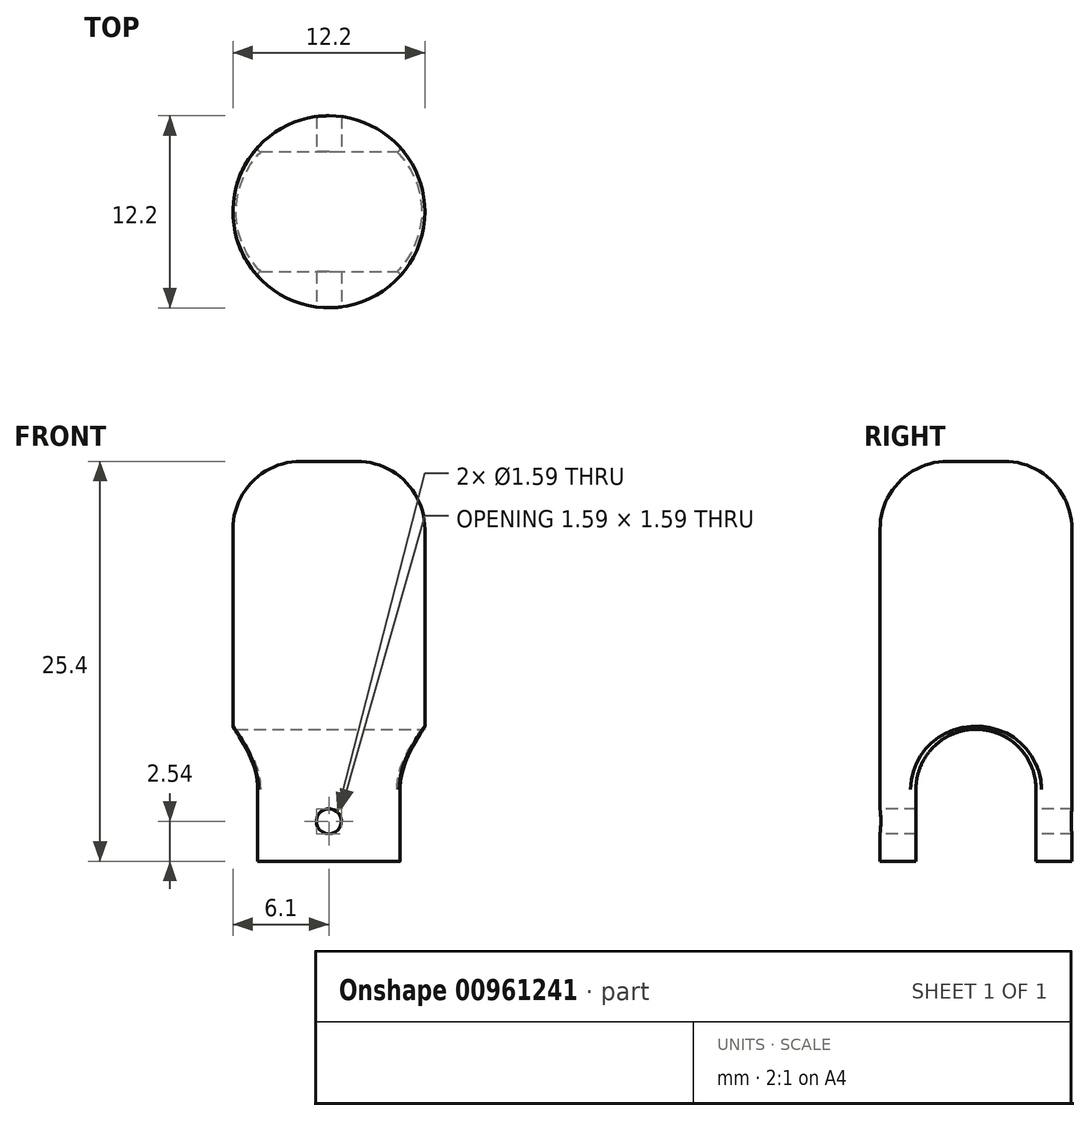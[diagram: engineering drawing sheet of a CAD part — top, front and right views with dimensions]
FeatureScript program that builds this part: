
annotation { "Feature Type Name" : "Feature", "Feature Type Description" : "" }
export const myFeature = defineFeature(function(context is Context, id is Id, definition is map)
    precondition{}
    {
        {
            var Q0;
            Q0=qCreatedBy(makeId("Top.planeOp"),FACE);
            var sketch = newSketch(context, id + "F0", { "sketchPlane" : qUnion([Q0])});
            skCircle(sketch, "E0", {"center": v(0, 0) * mm, "radius": 6.1 * mm});
            skSolve(sketch);
        }
        {
            var Q0;
            Q0 = qSketchRegion(id + "F0", true);
            extrude(context, id + "F1", {"entities" : qUnion([Q0]), "depth" : 25.4 * mm, "offsetDistance" : 25.4 * mm});
        }
        {
            var Q0;
            Q0=makeQuery(id+"F1.opExtrude","CAP_FACE",FACE,{"disambiguationData":[OSD([sQuery(id+"F0.wireOp",EDGE,"E0")])],"isStart":false});
            fillet(context, id + "F2", {"entities" : qUnion([Q0]), "radius" : 4.32 * mm, "tangentPropagation" : true, "allowEdgeOverflow" : false});
        }
        {
            var Q0;
            Q0=qCreatedBy(makeId("Front.planeOp"),FACE);
            var sketch = newSketch(context, id + "F3", { "sketchPlane" : qUnion([Q0])});
            skCircle(sketch, "E1", {"center": v(0, 2.54) * mm, "radius": 0.8 * mm});
            skSolve(sketch);
        }
        {
            var Q0;
            Q0 = qSketchRegion(id + "F3", true);
            extrude(context, id + "F4", {"entities" : qUnion([Q0]), "operationType" : NewBodyOperationType.REMOVE, "endBound" : BoundingType.THROUGH_ALL, "oppositeDirection" : true, "depth" : 25.4 * mm, "offsetDistance" : 25.4 * mm, "hasSecondDirection" : true, "secondDirectionBound" : SecondDirectionBoundingType.THROUGH_ALL, "secondDirectionOppositeDirection" : false, "secondDirectionDepth" : 25.4 * mm});
        }
        {
            var Q0;
            Q0=qCreatedBy(makeId("Right.planeOp"),FACE);
            var sketch = newSketch(context, id + "F5", { "sketchPlane" : qUnion([Q0])});
            skLineSegment(sketch, "E2", {"start": v(0, 0) * mm, "end": v(-3.81, 0) * mm});
            skLineSegment(sketch, "E3", {"start": v(-3.81, 0) * mm, "end": v(-3.81, 4.57) * mm});
            skLineSegment(sketch, "E4", {"start": v(0, 0) * mm, "end": v(3.81, 0) * mm});
            skLineSegment(sketch, "E5", {"start": v(3.81, 0) * mm, "end": v(3.81, 4.57) * mm});
            skArc(sketch, "E6", {"start": v(3.8, 4.57) * mm, "mid": v(0, 8.38) * mm, "end": v(-3.81, 4.57) * mm});
            skSolve(sketch);
        }
        {
            var Q0;
            Q0 = qSketchRegion(id + "F5", true);
            extrude(context, id + "F6", {"entities" : qUnion([Q0]), "operationType" : NewBodyOperationType.REMOVE, "endBound" : BoundingType.THROUGH_ALL, "oppositeDirection" : true, "depth" : 25.4 * mm, "offsetDistance" : 25.4 * mm, "hasSecondDirection" : true, "secondDirectionBound" : SecondDirectionBoundingType.THROUGH_ALL, "secondDirectionOppositeDirection" : false, "secondDirectionDepth" : 25.4 * mm});
        }
        {
            var Q0;
            Q0=makeQuery(id+"F6.boolean.opBoolean","INTERSECT",EDGE,{"disambiguationData":[OD(1.0)],"derivedFrom":[makeQuery(id+"F1.opExtrude","SWEPT_FACE",FACE,{"disambiguationData":[OSD([sQuery(id+"F0.wireOp",EDGE,"E0")])]}),makeQuery(id+"F6.opExtrude","SWEPT_FACE",FACE,{"disambiguationData":[OSD([sQuery(id+"F5.wireOp",EDGE,"E3")])]})]});
            var Q1;
            Q1=makeQuery(id+"F6.boolean.opBoolean","INTERSECT",EDGE,{"disambiguationData":[OD(1.0)],"derivedFrom":[makeQuery(id+"F1.opExtrude","SWEPT_FACE",FACE,{"disambiguationData":[OSD([sQuery(id+"F0.wireOp",EDGE,"E0")])]}),makeQuery(id+"F6.opExtrude","SWEPT_FACE",FACE,{"disambiguationData":[OSD([sQuery(id+"F5.wireOp",EDGE,"E6")])]})]});
            var Q2;
            Q2=makeQuery(id+"F6.boolean.opBoolean","INTERSECT",EDGE,{"disambiguationData":[OD(1.0)],"derivedFrom":[makeQuery(id+"F1.opExtrude","SWEPT_FACE",FACE,{"disambiguationData":[OSD([sQuery(id+"F0.wireOp",EDGE,"E0")])]}),makeQuery(id+"F6.opExtrude","SWEPT_FACE",FACE,{"disambiguationData":[OSD([sQuery(id+"F5.wireOp",EDGE,"E5")])]})]});
            var Q3;
            Q3=makeQuery(id+"F6.boolean.opBoolean","INTERSECT",EDGE,{"disambiguationData":[OD(0.0)],"derivedFrom":[makeQuery(id+"F1.opExtrude","SWEPT_FACE",FACE,{"disambiguationData":[OSD([sQuery(id+"F0.wireOp",EDGE,"E0")])]}),makeQuery(id+"F6.opExtrude","SWEPT_FACE",FACE,{"disambiguationData":[OSD([sQuery(id+"F5.wireOp",EDGE,"E6")])]})]});
            var Q4;
            Q4=makeQuery(id+"F6.boolean.opBoolean","INTERSECT",EDGE,{"disambiguationData":[OD(0.0)],"derivedFrom":[makeQuery(id+"F1.opExtrude","SWEPT_FACE",FACE,{"disambiguationData":[OSD([sQuery(id+"F0.wireOp",EDGE,"E0")])]}),makeQuery(id+"F6.opExtrude","SWEPT_FACE",FACE,{"disambiguationData":[OSD([sQuery(id+"F5.wireOp",EDGE,"E5")])]})]});
            fillet(context, id + "F7", {"entities" : qUnion([Q0, Q1, Q2, Q3, Q4]), "radius" : 0.2 * mm, "tangentPropagation" : true, "allowEdgeOverflow" : false});
        }
    });
